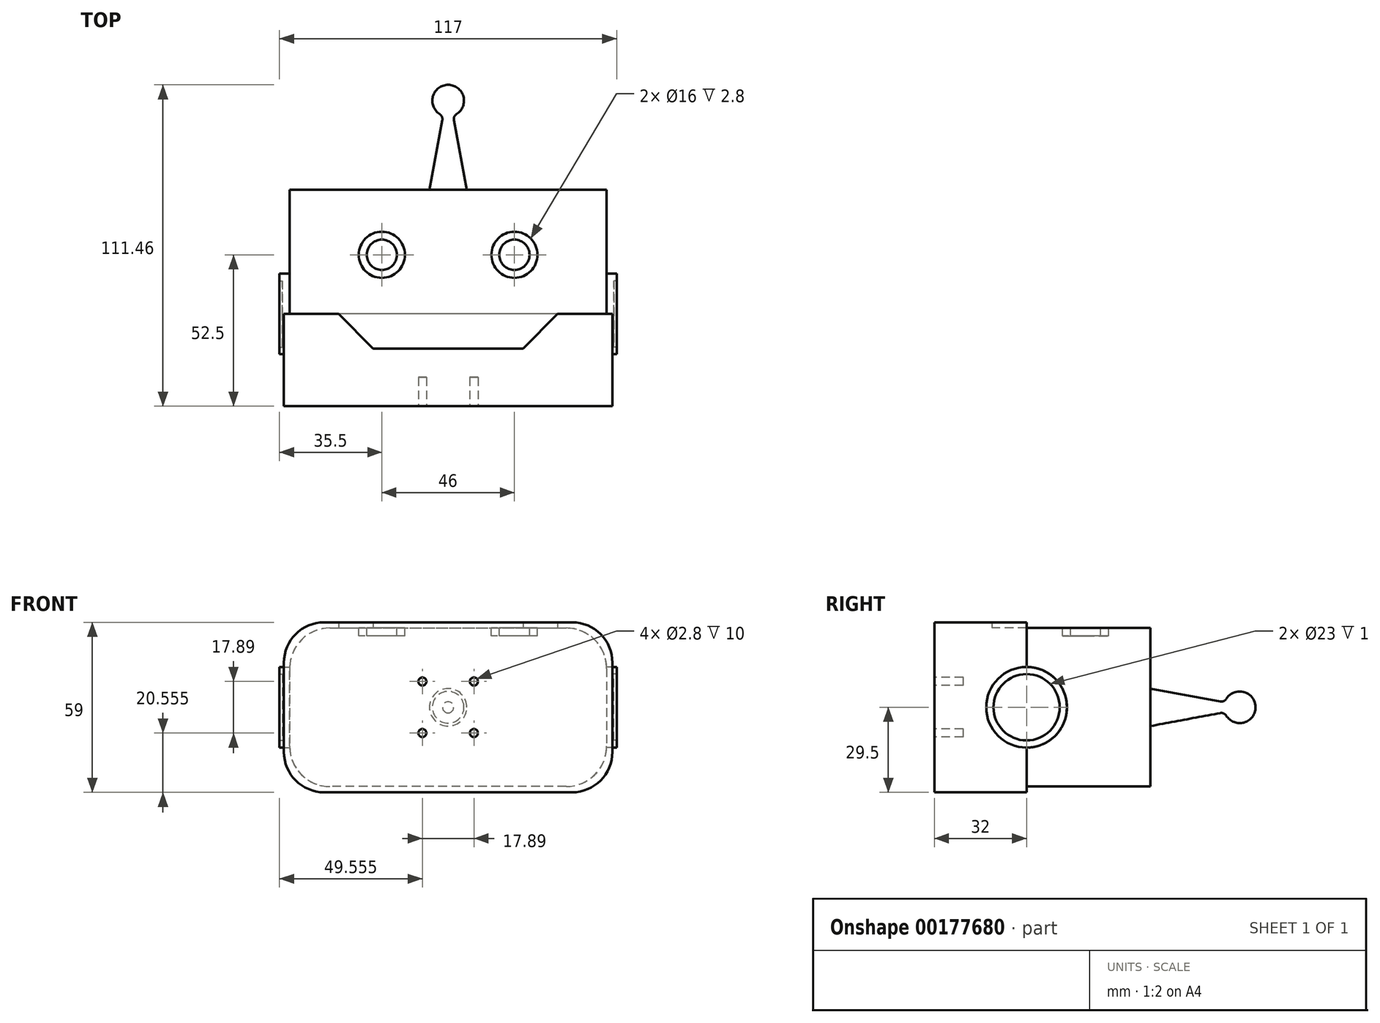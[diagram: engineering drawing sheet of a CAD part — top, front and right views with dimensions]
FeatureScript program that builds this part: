
annotation { "Feature Type Name" : "Feature", "Feature Type Description" : "" }
export const myFeature = defineFeature(function(context is Context, id is Id, definition is map)
    precondition{}
    {
        {
            var Q0;
            Q0=qCreatedBy(makeId("Top.planeOp"),FACE);
            var sketch = newSketch(context, id + "F0", { "sketchPlane" : qUnion([Q0])});
            skLineSegment(sketch, "E0.bottom", {"start": v(-55, 37.5) * mm, "end": v(55, 37.5) * mm});
            skLineSegment(sketch, "E0.top", {"start": v(-55, -37.5) * mm, "end": v(55, -37.5) * mm});
            skLineSegment(sketch, "E0.left", {"start": v(-55, 37.5) * mm, "end": v(-55, -37.5) * mm});
            skLineSegment(sketch, "E0.right", {"start": v(55, 37.5) * mm, "end": v(55, -37.5) * mm});
            skLineSegment(sketch, "E1", {"start": v(0, 37.5) * mm, "end": v(0, -37.5) * mm, "construction": true});
            skLineSegment(sketch, "E2", {"start": v(55, 0) * mm, "end": v(-55, 0) * mm, "construction": true});
            skSolve(sketch);
        }
        {
            var Q0;
            Q0=qSketchRegion(id+"F0",true);
            extrude(context, id + "F1", {"entities" : qUnion([Q0]), "depth" : 55 * mm});
        }
        {
            var Q0;
            Q0=makeQuery(id+"F1.opExtrude","CAP_FACE",FACE,{"disambiguationData":[OSD([sQuery(id+"F0.wireOp",EDGE,"E0.bottom"),sQuery(id+"F0.wireOp",EDGE,"E0.top"),sQuery(id+"F0.wireOp",EDGE,"E0.left"),sQuery(id+"F0.wireOp",EDGE,"E0.right")])],"isStart":false});
            var sketch = newSketch(context, id + "F2", { "sketchPlane" : qUnion([Q0])});
            skLineSegment(sketch, "E3", {"start": v(-55, -5.5) * mm, "end": v(-38, -5.5) * mm});
            skLineSegment(sketch, "E4", {"start": v(-38, -5.5) * mm, "end": v(-26, -17.54) * mm});
            skLineSegment(sketch, "E5", {"start": v(-26, -17.54) * mm, "end": v(26, -17.54) * mm});
            skLineSegment(sketch, "E6", {"start": v(26, -17.54) * mm, "end": v(38, -5.5) * mm});
            skLineSegment(sketch, "E7", {"start": v(38, -5.5) * mm, "end": v(55, -5.5) * mm});
            skLineSegment(sketch, "E8", {"start": v(0, 37.5) * mm, "end": v(0, -37.5) * mm});
            skLineSegment(sketch, "E9", {"start": v(26, -17.54) * mm, "end": v(0, -17.54) * mm});
            skLineSegment(sketch, "E10", {"start": v(0, -17.54) * mm, "end": v(-26, -17.54) * mm});
            skLineSegment(sketch, "E11", {"start": v(-26, -17.54) * mm, "end": v(0, -17.54) * mm});
            skSolve(sketch);
        }
        {
            var Q0;
            Q0=qSketchRegion(id+"F2",true);
            var Q1;
            Q1=makeQuery(id+"F2.imprint","IMPRINT",FACE,{"disambiguationData":[TD([[makeQuery(id+"F2.imprint","IMPRINT",EDGE,{"derivedFrom":sQuery(id+"F2.wireOp",EDGE,"E6")}),-1.0]])]});
            var Q2;
            {var subQ4=sQuery(id+"F2.wireOp",EDGE,"E3");Q2=makeQuery(id+"F2.imprint","IMPRINT",FACE,{"disambiguationData":[TD([[makeQuery(id+"F2.imprint","IMPRINT",EDGE,{"derivedFrom":subQ4}),-1.0]])]});}
            extrude(context, id + "F3", {"entities" : qUnion([Q0, Q1, Q2]), "operationType" : NewBodyOperationType.ADD, "depth" : 2 * mm});
        }
        {
            var Q0;
            {var subQ0=sQuery(id+"F0.wireOp",EDGE,"E0.right");Q0=makeQuery(id+"F3.boolean.opBoolean","MERGE",FACE,{"derivedFrom":[makeQuery(id+"F1.opExtrude","SWEPT_FACE",FACE,{"disambiguationData":[OSD([subQ0])]}),makeQuery(id+"F3.opExtrude","SWEPT_FACE",FACE,{"disambiguationData":[OSD([subQ0])]})]});}
            var sketch = newSketch(context, id + "F4", { "sketchPlane" : qUnion([Q0])});
            skLineSegment(sketch, "E12", {"start": v(-5.5, 55) * mm, "end": v(-5.5, 0) * mm});
            skLineSegment(sketch, "E13.0", {"start": v(37.5, 0) * mm, "end": v(-37.5, 0) * mm});
            skLineSegment(sketch, "E13.1", {"start": v(-37.5, 57) * mm, "end": v(-37.5, 0) * mm});
            skLineSegment(sketch, "E13.2", {"start": v(-5.5, 57) * mm, "end": v(-37.5, 57) * mm});
            skPoint(sketch, "E13.3", {"position": v(-5.5, 57) * mm});
            skLineSegment(sketch, "E13.4", {"start": v(-5.5, 57) * mm, "end": v(-5.5, 55) * mm});
            skSolve(sketch);
        }
        {
            var Q0;
            {var subQ2=sQuery(id+"F4.wireOp",EDGE,"E12");Q0=makeQuery(id+"F4.imprint","IMPRINT",FACE,{"disambiguationData":[TD([[makeQuery(id+"F4.imprint","IMPRINT",EDGE,{"derivedFrom":subQ2}),-1.0]])]});}
            extrude(context, id + "F5", {"entities" : qUnion([Q0]), "operationType" : NewBodyOperationType.ADD, "depth" : 2 * mm});
        }
        {
            var Q0;
            Q0=makeQuery(id+"F5.boolean.opBoolean","MERGE",FACE,{"derivedFrom":[makeQuery(id+"F1.opExtrude","CAP_FACE",FACE,{"disambiguationData":[OSD([sQuery(id+"F0.wireOp",EDGE,"E0.bottom"),sQuery(id+"F0.wireOp",EDGE,"E0.top"),sQuery(id+"F0.wireOp",EDGE,"E0.left"),sQuery(id+"F0.wireOp",EDGE,"E0.right")])],"isStart":true}),makeQuery(id+"F5.opExtrude","SWEPT_FACE",FACE,{"disambiguationData":[OSD([sQuery(id+"F4.wireOp",EDGE,"E13.0")])]})]});
            var sketch = newSketch(context, id + "F6", { "sketchPlane" : qUnion([Q0])});
            skLineSegment(sketch, "E14.bottom", {"start": v(57, 5.5) * mm, "end": v(-55, 5.5) * mm});
            skLineSegment(sketch, "E14.top", {"start": v(57, 37.5) * mm, "end": v(-55, 37.5) * mm});
            skLineSegment(sketch, "E14.left", {"start": v(57, 5.5) * mm, "end": v(57, 37.5) * mm});
            skLineSegment(sketch, "E14.right", {"start": v(-55, 5.5) * mm, "end": v(-55, 37.5) * mm});
            skSolve(sketch);
        }
        {
            var Q0;
            Q0=qSketchRegion(id+"F6",true);
            extrude(context, id + "F7", {"entities" : qUnion([Q0]), "operationType" : NewBodyOperationType.ADD, "depth" : 2 * mm});
        }
        {
            var Q0;
            {var subQ0=sQuery(id+"F0.wireOp",EDGE,"E0.left");Q0=makeQuery(id+"F7.boolean.opBoolean","MERGE",FACE,{"derivedFrom":[makeQuery(id+"F3.boolean.opBoolean","MERGE",FACE,{"derivedFrom":[makeQuery(id+"F1.opExtrude","SWEPT_FACE",FACE,{"disambiguationData":[OSD([subQ0])]}),makeQuery(id+"F3.opExtrude","SWEPT_FACE",FACE,{"disambiguationData":[OSD([subQ0])]})]}),makeQuery(id+"F7.opExtrude","SWEPT_FACE",FACE,{"disambiguationData":[OSD([sQuery(id+"F6.wireOp",EDGE,"E14.right")])]})]});}
            var sketch = newSketch(context, id + "F8", { "sketchPlane" : qUnion([Q0])});
            skLineSegment(sketch, "E15.bottom", {"start": v(5.5, -2) * mm, "end": v(37.5, -2) * mm});
            skLineSegment(sketch, "E15.top", {"start": v(5.5, 57) * mm, "end": v(37.5, 57) * mm});
            skLineSegment(sketch, "E15.left", {"start": v(5.5, -2) * mm, "end": v(5.5, 57) * mm});
            skLineSegment(sketch, "E15.right", {"start": v(37.5, -2) * mm, "end": v(37.5, 57) * mm});
            skSolve(sketch);
        }
        {
            var Q0;
            Q0=qSketchRegion(id+"F8",true);
            extrude(context, id + "F9", {"entities" : qUnion([Q0]), "operationType" : NewBodyOperationType.ADD, "depth" : 2 * mm});
        }
        {
            var Q0;
            Q0=makeQuery(id+"F9.opExtrude","CAP_EDGE",EDGE,{"disambiguationData":[OSD([sQuery(id+"F8.wireOp",EDGE,"E15.top")])],"isStart":false});
            var Q1;
            Q1=makeQuery(id+"F1.opExtrude","CAP_EDGE",EDGE,{"disambiguationData":[OSD([sQuery(id+"F0.wireOp",EDGE,"E0.left")])],"isStart":false});
            var Q2;
            Q2=makeQuery(id+"F5.opExtrude","CAP_EDGE",EDGE,{"disambiguationData":[OSD([sQuery(id+"F4.wireOp",EDGE,"E13.2")])],"isStart":false});
            var Q3;
            Q3=makeQuery(id+"F1.opExtrude","CAP_EDGE",EDGE,{"disambiguationData":[OSD([sQuery(id+"F0.wireOp",EDGE,"E0.right")])],"isStart":false});
            var Q4;
            Q4=makeQuery(id+"F7.opExtrude","CAP_EDGE",EDGE,{"disambiguationData":[OSD([sQuery(id+"F6.wireOp",EDGE,"E14.left")])],"isStart":false});
            var Q5;
            Q5=makeQuery(id+"F1.opExtrude","CAP_EDGE",EDGE,{"disambiguationData":[OSD([sQuery(id+"F0.wireOp",EDGE,"E0.right")])],"isStart":true});
            var Q6;
            Q6=makeQuery(id+"F1.opExtrude","CAP_EDGE",EDGE,{"disambiguationData":[OSD([sQuery(id+"F0.wireOp",EDGE,"E0.left")])],"isStart":true});
            var Q7;
            Q7=makeQuery(id+"F9.opExtrude","CAP_EDGE",EDGE,{"disambiguationData":[OSD([sQuery(id+"F8.wireOp",EDGE,"E15.bottom")])],"isStart":false});
            fillet(context, id + "F10", {"entities" : qUnion([Q0, Q1, Q2, Q3, Q4, Q5, Q6, Q7]), "radius" : 14 * mm, "tangentPropagation" : true, "allowEdgeOverflow" : false});
        }
        {
            var Q0;
            Q0=makeQuery(id+"F1.opExtrude","CAP_FACE",FACE,{"disambiguationData":[OSD([sQuery(id+"F0.wireOp",EDGE,"E0.bottom"),sQuery(id+"F0.wireOp",EDGE,"E0.top"),sQuery(id+"F0.wireOp",EDGE,"E0.left"),sQuery(id+"F0.wireOp",EDGE,"E0.right")])],"isStart":false});
            var sketch = newSketch(context, id + "F11", { "sketchPlane" : qUnion([Q0])});
            skCircle(sketch, "E16", {"center": v(23, 15) * mm, "radius": 8 * mm});
            skCircle(sketch, "E17", {"center": v(-23, 15) * mm, "radius": 8 * mm});
            skLineSegment(sketch, "E18", {"start": v(41, 15) * mm, "end": v(-41, 15) * mm, "construction": true});
            skPoint(sketch, "E19", {"position": v(0, 15) * mm});
            skCircle(sketch, "E20", {"center": v(-23, 15) * mm, "radius": 5.25 * mm});
            skCircle(sketch, "E21", {"center": v(23, 15) * mm, "radius": 5.25 * mm});
            skLineSegment(sketch, "E22", {"start": v(-19.3, 17.7) * mm, "end": v(-19.3, 37.5) * mm});
            skSolve(sketch);
        }
        {
            var Q0;
            Q0=makeQuery(id+"F11.imprint","IMPRINT",FACE,{"disambiguationData":[TD([[makeQuery(id+"F11.imprint","IMPRINT",EDGE,{"derivedFrom":sQuery(id+"F11.wireOp",EDGE,"E17")}),1.0]])]});
            var Q1;
            Q1=makeQuery(id+"F11.imprint","IMPRINT",FACE,{"disambiguationData":[TD([[makeQuery(id+"F11.imprint","IMPRINT",EDGE,{"derivedFrom":sQuery(id+"F11.wireOp",EDGE,"mXLlLpRG-OS2o-uGzv-h3xE-d8vGsaIcWihP")}),1.0]])]});
            var Q2;
            Q2=makeQuery(id+"F11.imprint","IMPRINT",FACE,{"disambiguationData":[TD([[makeQuery(id+"F11.imprint","IMPRINT",EDGE,{"derivedFrom":sQuery(id+"F11.wireOp",EDGE,"E16")}),1.0]])]});
            var Q3;
            Q3=makeQuery(id+"F11.imprint","IMPRINT",FACE,{"disambiguationData":[TD([[makeQuery(id+"F11.imprint","IMPRINT",EDGE,{"derivedFrom":sQuery(id+"F11.wireOp",EDGE,"bwpR8pbf-H368-XPyx-2mUK-IzQucSXIfuzO")}),1.0]])]});
            extrude(context, id + "F12", {"entities" : qUnion([Q0, Q1, Q2, Q3]), "operationType" : NewBodyOperationType.REMOVE, "oppositeDirection" : true, "depth" : 2.8 * mm});
        }
        {
            var Q0;
            Q0=qCreatedBy(makeId("Right.planeOp"),FACE);
            var sketch = newSketch(context, id + "F13", { "sketchPlane" : qUnion([Q0])});
            skLineSegment(sketch, "E23", {"start": v(37.5, 27.5) * mm, "end": v(72.5, 27.5) * mm});
            skLineSegment(sketch, "E24", {"start": v(61.73, 29.5) * mm, "end": v(37.5, 34) * mm});
            skLineSegment(sketch, "E25", {"start": v(37.5, 34) * mm, "end": v(37.5, 27.5) * mm});
            skPoint(sketch, "E26", {"position": v(37.5, 27.5) * mm});
            skArc(sketch, "E27", {"start": v(73.96, 27.5) * mm, "mid": v(69.97, 32.79) * mm, "end": v(63.8, 30.4) * mm});
            skLineSegment(sketch, "E28", {"start": v(73.96, 27.5) * mm, "end": v(62.96, 27.5) * mm});
            skPoint(sketch, "E29.visualSharp", {"position": v(63.24, 29.22) * mm});
            skArc(sketch, "E29.filletArc", {"start": v(61.73, 29.5) * mm, "mid": v(62.9, 29.64) * mm, "end": v(63.8, 30.4) * mm});
            skSolve(sketch);
        }
        {
            var Q0;
            Q0=qSketchRegion(id+"F13",true);
            var Q1;
            Q1=sQuery(id+"F13.wireOp",EDGE,"E23");
            revolve(context, id + "F14", {"operationType" : NewBodyOperationType.ADD, "entities" : qUnion([Q0]), "axis" : qUnion([Q1]), "revolveType" : RevolveType.FULL});
        }
        {
            var Q0;
            {var subQ0=sQuery(id+"F0.wireOp",EDGE,"E0.top");Q0=makeQuery(id+"F9.boolean.opBoolean","MERGE",FACE,{"derivedFrom":[makeQuery(id+"F7.boolean.opBoolean","MERGE",FACE,{"derivedFrom":[makeQuery(id+"F5.boolean.opBoolean","MERGE",FACE,{"derivedFrom":[makeQuery(id+"F3.boolean.opBoolean","MERGE",FACE,{"derivedFrom":[makeQuery(id+"F1.opExtrude","SWEPT_FACE",FACE,{"disambiguationData":[OSD([subQ0])]}),makeQuery(id+"F3.opExtrude","SWEPT_FACE",FACE,{"disambiguationData":[OSD([subQ0])]})]}),makeQuery(id+"F5.opExtrude","SWEPT_FACE",FACE,{"disambiguationData":[OSD([sQuery(id+"F4.wireOp",EDGE,"E13.1")])]})]}),makeQuery(id+"F7.opExtrude","SWEPT_FACE",FACE,{"disambiguationData":[OSD([sQuery(id+"F6.wireOp",EDGE,"E14.top")])]})]}),makeQuery(id+"F9.opExtrude","SWEPT_FACE",FACE,{"disambiguationData":[OSD([sQuery(id+"F8.wireOp",EDGE,"E15.right")])]})]});}
            var sketch = newSketch(context, id + "F15", { "sketchPlane" : qUnion([Q0])});
            skCircle(sketch, "E30", {"center": v(0, 27.5) * mm, "radius": 17.5 * mm});
            skLineSegment(sketch, "E31", {"start": v(-8.94, 36.44) * mm, "end": v(0, 27.5) * mm});
            skLineSegment(sketch, "E32", {"start": v(0, 27.5) * mm, "end": v(8.94, 18.56) * mm});
            skLineSegment(sketch, "E33", {"start": v(0, 27.5) * mm, "end": v(8.94, 36.44) * mm});
            skLineSegment(sketch, "E34", {"start": v(0, 27.5) * mm, "end": v(-8.94, 18.56) * mm});
            skLineSegment(sketch, "E35", {"start": v(0, 27.5) * mm, "end": v(0, 0) * mm});
            skLineSegment(sketch, "E36", {"start": v(0, 45) * mm, "end": v(0, 57) * mm});
            skLineSegment(sketch, "E37", {"start": v(0, 10) * mm, "end": v(0, -2) * mm});
            skCircle(sketch, "E38", {"center": v(8.94, 18.56) * mm, "radius": 1.4 * mm});
            skCircle(sketch, "E39", {"center": v(8.94, 36.44) * mm, "radius": 1.4 * mm});
            skCircle(sketch, "E40", {"center": v(-8.94, 36.44) * mm, "radius": 1.4 * mm});
            skCircle(sketch, "E41", {"center": v(-8.94, 18.56) * mm, "radius": 1.4 * mm});
            skSolve(sketch);
        }
        {
            var Q0;
            Q0=makeQuery(id+"F15.imprint","IMPRINT",FACE,{"disambiguationData":[TD([[makeQuery(id+"F15.imprint","IMPRINT",EDGE,{"derivedFrom":sQuery(id+"F15.wireOp",EDGE,"E40")}),1.0]])]});
            var Q1;
            Q1=makeQuery(id+"F15.imprint","IMPRINT",FACE,{"disambiguationData":[TD([[makeQuery(id+"F15.imprint","IMPRINT",EDGE,{"derivedFrom":sQuery(id+"F15.wireOp",EDGE,"E39")}),1.0]])]});
            var Q2;
            Q2=makeQuery(id+"F15.imprint","IMPRINT",FACE,{"disambiguationData":[TD([[makeQuery(id+"F15.imprint","IMPRINT",EDGE,{"derivedFrom":sQuery(id+"F15.wireOp",EDGE,"E38")}),1.0]])]});
            var Q3;
            Q3=makeQuery(id+"F15.imprint","IMPRINT",FACE,{"disambiguationData":[TD([[makeQuery(id+"F15.imprint","IMPRINT",EDGE,{"derivedFrom":sQuery(id+"F15.wireOp",EDGE,"E41")}),1.0]])]});
            extrude(context, id + "F16", {"entities" : qUnion([Q0, Q1, Q2, Q3]), "operationType" : NewBodyOperationType.REMOVE, "oppositeDirection" : true, "depth" : 10 * mm});
        }
        {
            var Q0;
            {var subQ0=sQuery(id+"F0.wireOp",EDGE,"E0.right");Q0=makeQuery(id+"F3.boolean.opBoolean","MERGE",FACE,{"derivedFrom":[makeQuery(id+"F1.opExtrude","SWEPT_FACE",FACE,{"disambiguationData":[OSD([subQ0])]}),makeQuery(id+"F3.opExtrude","SWEPT_FACE",FACE,{"disambiguationData":[OSD([subQ0])]})]});}
            var sketch = newSketch(context, id + "F17", { "sketchPlane" : qUnion([Q0])});
            skCircle(sketch, "E42", {"center": v(-5.5, 27.5) * mm, "radius": 14 * mm});
            skCircle(sketch, "E43", {"center": v(-5.5, 27.5) * mm, "radius": 11.5 * mm});
            skSolve(sketch);
        }
        {
            var Q0;
            Q0=qSketchRegion(id+"F17",true);
            extrude(context, id + "F18", {"entities" : qUnion([Q0]), "operationType" : NewBodyOperationType.ADD, "depth" : 3.5 * mm});
        }
        {
            var Q0;
            {var subQ0=sQuery(id+"F17.wireOp",EDGE,"E43");var subQ1=makeQuery(id+"F5.opExtrude","CAP_EDGE",EDGE,{"disambiguationData":[OSD([sQuery(id+"F4.wireOp",EDGE,"E12"),sQuery(id+"F4.wireOp",EDGE,"E13.4")])],"isStart":true});var subQ2=makeQuery(id+"F17.imprint","INTERSECT",VERTEX,{"disambiguationData":[OD(0.0)],"derivedFrom":[subQ1,subQ0]});Q0=makeQuery(id+"F17.imprint","IMPRINT",FACE,{"disambiguationData":[TD([[makeQuery(id+"F17.imprint","IMPRINT",EDGE,{"disambiguationData":[TD([[subQ2,1.0]])],"derivedFrom":subQ0}),1.0]])]});}
            extrude(context, id + "F19", {"entities" : qUnion([Q0]), "operationType" : NewBodyOperationType.ADD, "depth" : 2.5 * mm});
        }
        {
            var Q0;
            {var subQ0=sQuery(id+"F4.wireOp",EDGE,"E13.4");var subQ1=sQuery(id+"F4.wireOp",EDGE,"E12");Q0=makeQuery(id+"F18.boolean.opBoolean","SPLIT",FACE,{"disambiguationData":[TD([makeQuery(id+"F18.opExtrude","SWEPT_FACE",FACE,{"disambiguationData":[OSD([sQuery(id+"F17.wireOp",EDGE,"E43")])]})])],"derivedFrom":makeQuery(id+"F7.boolean.opBoolean","MERGE",FACE,{"derivedFrom":[makeQuery(id+"F5.opExtrude","CAP_FACE",FACE,{"disambiguationData":[OSD([subQ1,sQuery(id+"F4.wireOp",EDGE,"E13.0"),sQuery(id+"F4.wireOp",EDGE,"E13.1"),sQuery(id+"F4.wireOp",EDGE,"E13.2"),subQ0])],"isStart":false}),makeQuery(id+"F7.opExtrude","SWEPT_FACE",FACE,{"disambiguationData":[OSD([sQuery(id+"F6.wireOp",EDGE,"E14.left")])]})]})});}
            extrude(context, id + "F20", {"entities" : qUnion([Q0]), "operationType" : NewBodyOperationType.ADD, "depth" : .5 * mm});
        }
        {
            var Q0;
            {var subQ0=sQuery(id+"F0.wireOp",EDGE,"E0.left");Q0=makeQuery(id+"F7.boolean.opBoolean","MERGE",FACE,{"derivedFrom":[makeQuery(id+"F3.boolean.opBoolean","MERGE",FACE,{"derivedFrom":[makeQuery(id+"F1.opExtrude","SWEPT_FACE",FACE,{"disambiguationData":[OSD([subQ0])]}),makeQuery(id+"F3.opExtrude","SWEPT_FACE",FACE,{"disambiguationData":[OSD([subQ0])]})]}),makeQuery(id+"F7.opExtrude","SWEPT_FACE",FACE,{"disambiguationData":[OSD([sQuery(id+"F6.wireOp",EDGE,"E14.right")])]})]});}
            var sketch = newSketch(context, id + "F21", { "sketchPlane" : qUnion([Q0])});
            skCircle(sketch, "E44.0", {"center": v(5.5, 27.5) * mm, "radius": 14 * mm});
            skCircle(sketch, "E44.1", {"center": v(5.5, 27.5) * mm, "radius": 11.5 * mm});
            skSolve(sketch);
        }
        {
            var Q0;
            Q0=qSketchRegion(id+"F21",true);
            extrude(context, id + "F22", {"entities" : qUnion([Q0]), "operationType" : NewBodyOperationType.ADD, "depth" : 3.5 * mm});
        }
        {
            var Q0;
            {var subQ0=sQuery(id+"F8.wireOp",EDGE,"E15.left");Q0=makeQuery(id+"F22.boolean.opBoolean","SPLIT",FACE,{"disambiguationData":[TD([makeQuery(id+"F22.opExtrude","SWEPT_FACE",FACE,{"disambiguationData":[OSD([sQuery(id+"F21.wireOp",EDGE,"E44.1")])]})])],"derivedFrom":makeQuery(id+"F9.opExtrude","CAP_FACE",FACE,{"disambiguationData":[OSD([sQuery(id+"F8.wireOp",EDGE,"E15.bottom"),sQuery(id+"F8.wireOp",EDGE,"E15.top"),subQ0,sQuery(id+"F8.wireOp",EDGE,"E15.right")])],"isStart":false})});}
            extrude(context, id + "F23", {"entities" : qUnion([Q0]), "operationType" : NewBodyOperationType.ADD, "depth" : .5 * mm});
        }
        {
            var Q0;
            {var subQ0=sQuery(id+"F0.wireOp",EDGE,"E0.left");Q0=makeQuery(id+"F22.boolean.opBoolean","SPLIT",FACE,{"disambiguationData":[TD([makeQuery(id+"F3.opExtrude","SWEPT_FACE",FACE,{"disambiguationData":[OSD([sQuery(id+"F2.wireOp",EDGE,"E3")])]})])],"derivedFrom":makeQuery(id+"F7.boolean.opBoolean","MERGE",FACE,{"derivedFrom":[makeQuery(id+"F3.boolean.opBoolean","MERGE",FACE,{"derivedFrom":[makeQuery(id+"F1.opExtrude","SWEPT_FACE",FACE,{"disambiguationData":[OSD([subQ0])]}),makeQuery(id+"F3.opExtrude","SWEPT_FACE",FACE,{"disambiguationData":[OSD([subQ0])]})]}),makeQuery(id+"F7.opExtrude","SWEPT_FACE",FACE,{"disambiguationData":[OSD([sQuery(id+"F6.wireOp",EDGE,"E14.right")])]})]})});}
            extrude(context, id + "F24", {"entities" : qUnion([Q0]), "operationType" : NewBodyOperationType.ADD, "depth" : 2.5 * mm});
        }
    });
